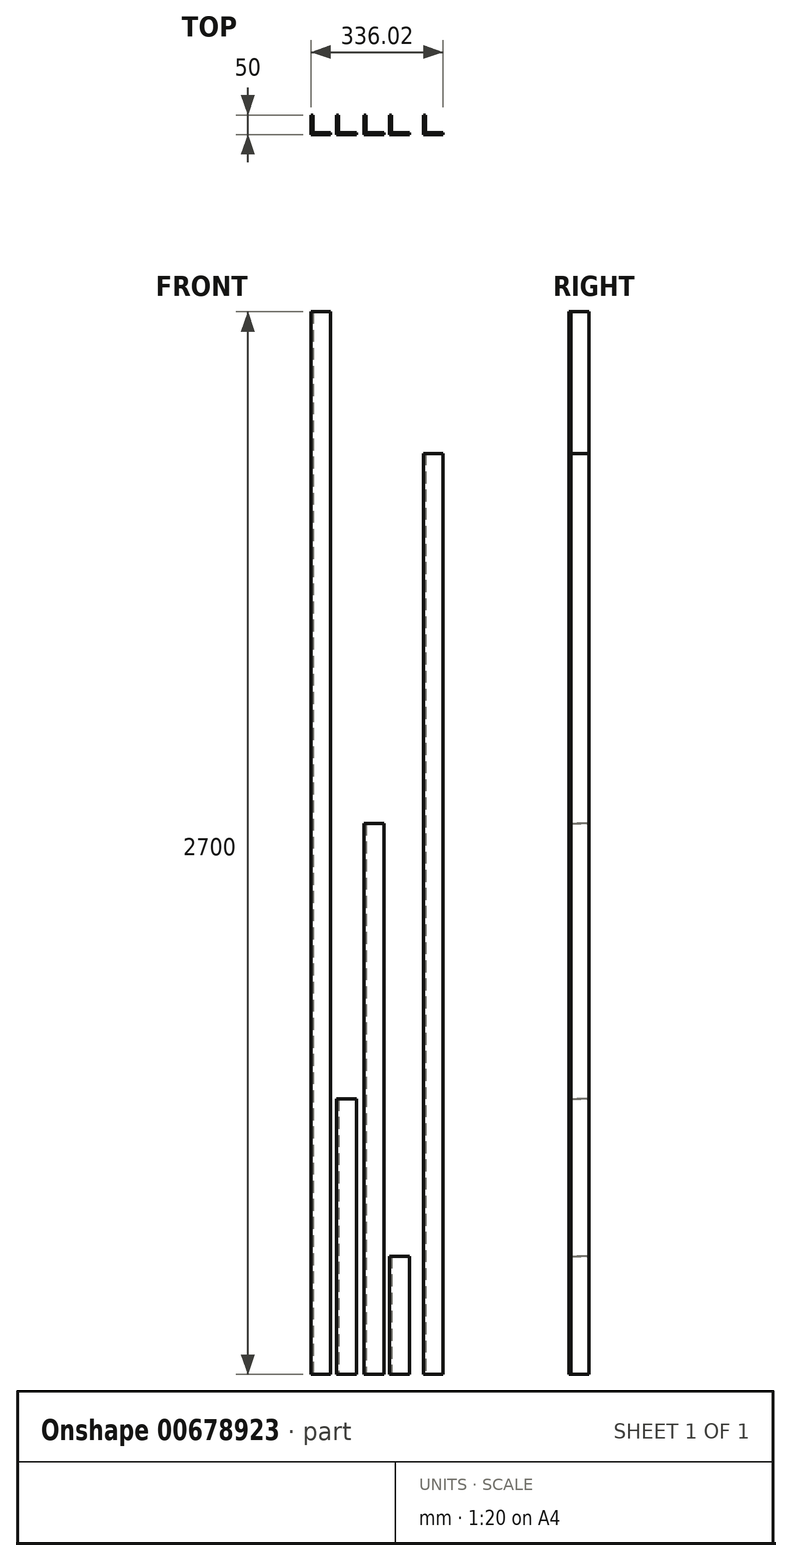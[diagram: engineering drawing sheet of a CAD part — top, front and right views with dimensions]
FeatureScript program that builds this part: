
annotation { "Feature Type Name" : "Feature", "Feature Type Description" : "" }
export const myFeature = defineFeature(function(context is Context, id is Id, definition is map)
    precondition{}
    {
        {
            var Q0;
            Q0=qCreatedBy(makeId("Top.planeOp"),FACE);
            var sketch = newSketch(context, id + "F0", { "sketchPlane" : qUnion([Q0])});
            skLineSegment(sketch, "E0", {"start": v(0, 0) * mm, "end": v(0, 50) * mm});
            skLineSegment(sketch, "E1", {"start": v(0, 50) * mm, "end": v(5, 50) * mm});
            skLineSegment(sketch, "E2", {"start": v(5, 50) * mm, "end": v(5, 5) * mm});
            skLineSegment(sketch, "E3", {"start": v(5, 5) * mm, "end": v(50, 5) * mm});
            skLineSegment(sketch, "E4", {"start": v(50, 5) * mm, "end": v(50, 0) * mm});
            skLineSegment(sketch, "E5", {"start": v(50, 0) * mm, "end": v(0, 0) * mm});
            skSolve(sketch);
        }
        {
            var Q0;
            Q0=qSketchRegion(id+"F0",true);
            extrude(context, id + "F1", {"entities" : qUnion([Q0]), "depth" : 2700 * mm, "offsetDistance" : 25 * mm});
        }
        {
            var Q0;
            Q0=qCreatedBy(makeId("Top.planeOp"),FACE);
            var sketch = newSketch(context, id + "F2", { "sketchPlane" : qUnion([Q0])});
            skLineSegment(sketch, "E6", {"start": v(65.43, 0) * mm, "end": v(65.43, 50) * mm});
            skLineSegment(sketch, "E7", {"start": v(65.43, 50) * mm, "end": v(70.43, 50) * mm});
            skLineSegment(sketch, "E8", {"start": v(70.43, 50) * mm, "end": v(70.43, 5) * mm});
            skLineSegment(sketch, "E9", {"start": v(70.43, 5) * mm, "end": v(115.43, 5) * mm});
            skLineSegment(sketch, "E10", {"start": v(115.43, 5) * mm, "end": v(115.43, 0) * mm});
            skLineSegment(sketch, "E11", {"start": v(115.43, 0) * mm, "end": v(65.43, 0) * mm});
            skSolve(sketch);
        }
        {
            var Q0;
            Q0=qSketchRegion(id+"F2",true);
            extrude(context, id + "F3", {"entities" : qUnion([Q0]), "depth" : 700 * mm, "offsetDistance" : 25 * mm});
        }
        {
            var Q0;
            Q0=qCreatedBy(makeId("Top.planeOp"),FACE);
            var sketch = newSketch(context, id + "F4", { "sketchPlane" : qUnion([Q0])});
            skLineSegment(sketch, "E12", {"start": v(135.33, 0) * mm, "end": v(135.33, 50) * mm});
            skLineSegment(sketch, "E13", {"start": v(135.33, 50) * mm, "end": v(140.33, 50) * mm});
            skLineSegment(sketch, "E14", {"start": v(140.33, 50) * mm, "end": v(140.33, 5) * mm});
            skLineSegment(sketch, "E15", {"start": v(140.33, 5) * mm, "end": v(185.33, 5) * mm});
            skLineSegment(sketch, "E16", {"start": v(185.33, 5) * mm, "end": v(185.33, 0) * mm});
            skLineSegment(sketch, "E17", {"start": v(185.33, 0) * mm, "end": v(135.33, 0) * mm});
            skSolve(sketch);
        }
        {
            var Q0;
            Q0=qCreatedBy(makeId("Top.planeOp"),FACE);
            var sketch = newSketch(context, id + "F5", { "sketchPlane" : qUnion([Q0])});
            skLineSegment(sketch, "E18", {"start": v(200.4, 0) * mm, "end": v(200.4, 50) * mm});
            skLineSegment(sketch, "E19", {"start": v(200.4, 50) * mm, "end": v(205.4, 50) * mm});
            skLineSegment(sketch, "E20", {"start": v(205.4, 50) * mm, "end": v(205.4, 5) * mm});
            skLineSegment(sketch, "E21", {"start": v(205.4, 5) * mm, "end": v(250.4, 5) * mm});
            skLineSegment(sketch, "E22", {"start": v(250.4, 5) * mm, "end": v(250.4, 0) * mm});
            skLineSegment(sketch, "E23", {"start": v(250.4, 0) * mm, "end": v(200.4, 0) * mm});
            skSolve(sketch);
        }
        {
            var Q0;
            Q0=qSketchRegion(id+"F4",true);
            extrude(context, id + "F6", {"entities" : qUnion([Q0]), "depth" : 1400 * mm, "offsetDistance" : 25 * mm});
        }
        {
            var Q0;
            Q0=qSketchRegion(id+"F5",true);
            extrude(context, id + "F7", {"entities" : qUnion([Q0]), "depth" : 300 * mm, "offsetDistance" : 25 * mm});
        }
        {
            var Q0;
            Q0=qCreatedBy(makeId("Top.planeOp"),FACE);
            var sketch = newSketch(context, id + "F8", { "sketchPlane" : qUnion([Q0])});
            skLineSegment(sketch, "E24", {"start": v(286.02, 0) * mm, "end": v(286.02, 50) * mm});
            skLineSegment(sketch, "E25", {"start": v(286.02, 50) * mm, "end": v(291.02, 50) * mm});
            skLineSegment(sketch, "E26", {"start": v(291.02, 50) * mm, "end": v(291.02, 5) * mm});
            skLineSegment(sketch, "E27", {"start": v(291.02, 5) * mm, "end": v(336.02, 5) * mm});
            skLineSegment(sketch, "E28", {"start": v(336.02, 5) * mm, "end": v(336.02, 0) * mm});
            skLineSegment(sketch, "E29", {"start": v(336.02, 0) * mm, "end": v(286.02, 0) * mm});
            skSolve(sketch);
        }
        {
            var Q0;
            Q0=qSketchRegion(id+"F8",true);
            extrude(context, id + "F9", {"entities" : qUnion([Q0]), "depth" : 2340 * mm, "offsetDistance" : 25 * mm});
        }
    });
